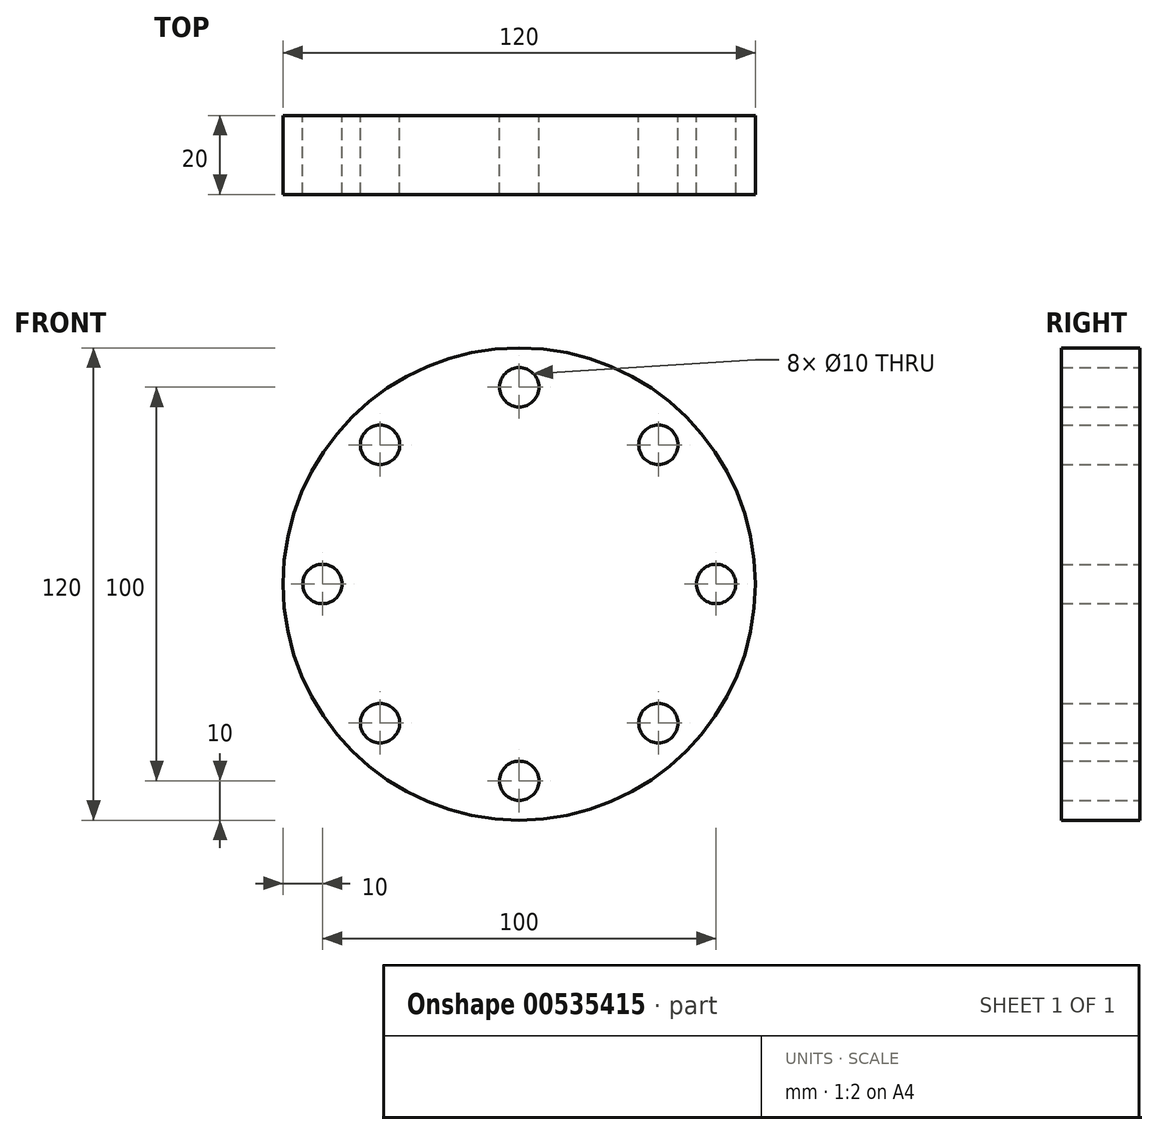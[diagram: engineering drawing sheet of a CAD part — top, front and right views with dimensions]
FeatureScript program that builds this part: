
annotation { "Feature Type Name" : "Feature", "Feature Type Description" : "" }
export const myFeature = defineFeature(function(context is Context, id is Id, definition is map)
    precondition{}
    {
        {
            var Q0;
            Q0=qCreatedBy(makeId("Front.planeOp"),FACE);
            var sketch = newSketch(context, id + "F0", { "sketchPlane" : qUnion([Q0])});
            skCircle(sketch, "E0", {"center": v(0, 0) * mm, "radius": 60 * mm});
            skCircle(sketch, "E1", {"center": v(0, 50) * mm, "radius": 5 * mm});
            skCircle(sketch, "E2.1.0", {"center": v(-35.36, 35.36) * mm, "radius": 5 * mm});
            skCircle(sketch, "E2.2.0", {"center": v(-50, 0) * mm, "radius": 5 * mm});
            skCircle(sketch, "E2.3.0", {"center": v(-35.36, -35.36) * mm, "radius": 5 * mm});
            skCircle(sketch, "E2.4.0", {"center": v(0, -50) * mm, "radius": 5 * mm});
            skCircle(sketch, "E2.5.0", {"center": v(35.36, -35.36) * mm, "radius": 5 * mm});
            skCircle(sketch, "E2.6.0", {"center": v(50, 0) * mm, "radius": 5 * mm});
            skCircle(sketch, "E2.7.0", {"center": v(35.36, 35.36) * mm, "radius": 5 * mm});
            skSolve(sketch);
        }
        {
            var Q0;
            Q0 = qSketchRegion(id + "F0", true);
            extrude(context, id + "F1", {"entities" : qUnion([Q0]), "depth" : 20 * mm, "offsetDistance" : 25 * mm});
        }
    });
